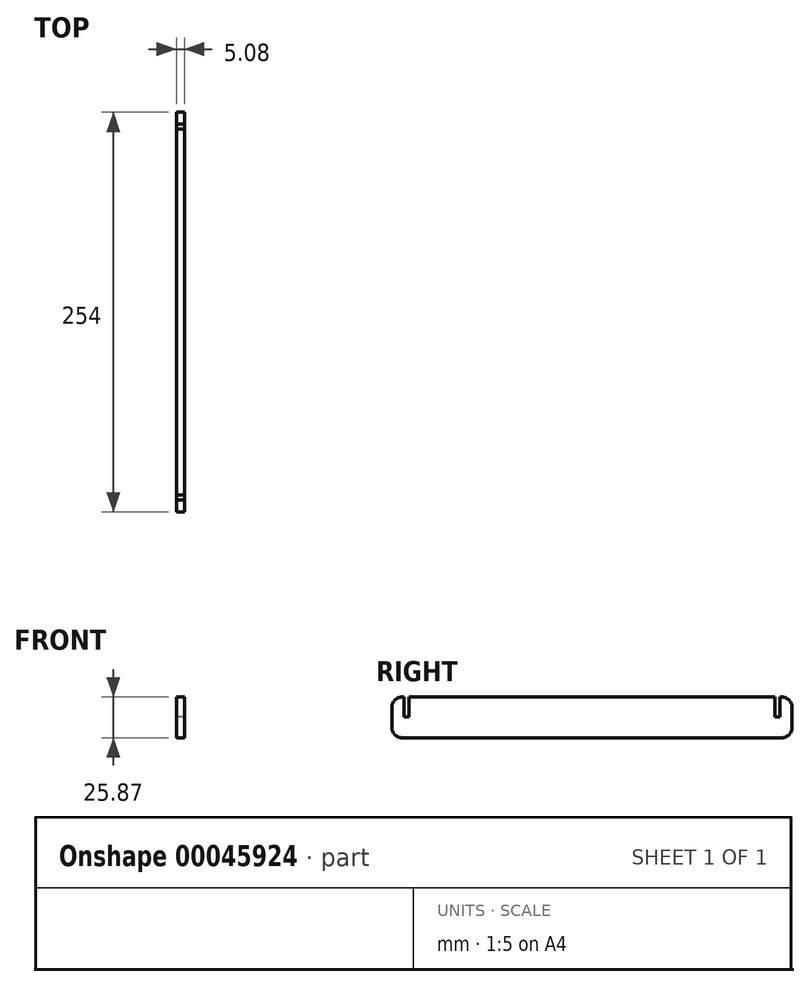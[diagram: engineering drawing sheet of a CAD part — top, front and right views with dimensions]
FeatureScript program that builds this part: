
annotation { "Feature Type Name" : "Feature", "Feature Type Description" : "" }
export const myFeature = defineFeature(function(context is Context, id is Id, definition is map)
    precondition{}
    {
        {
            var Q0;
            Q0=qCreatedBy(makeId("Right.planeOp"),FACE);
            var sketch = newSketch(context, id + "F0", { "sketchPlane" : qUnion([Q0])});
            skLineSegment(sketch, "E0.bottom", {"start": v(6.35, 0) * mm, "end": v(247.65, 0) * mm});
            skLineSegment(sketch, "E0.top", {"start": v(6.35, 25.87) * mm, "end": v(7.62, 25.87) * mm});
            skLineSegment(sketch, "E0.left", {"start": v(0, 6.35) * mm, "end": v(0, 19.52) * mm});
            skLineSegment(sketch, "E0.right", {"start": v(254, 6.35) * mm, "end": v(254, 19.52) * mm});
            skLineSegment(sketch, "E1.top", {"start": v(7.62, 13.17) * mm, "end": v(10.8, 13.17) * mm});
            skLineSegment(sketch, "E1.left", {"start": v(7.62, 25.87) * mm, "end": v(7.62, 13.17) * mm});
            skLineSegment(sketch, "E1.right", {"start": v(10.8, 25.87) * mm, "end": v(10.8, 13.17) * mm});
            skLineSegment(sketch, "E2.top", {"start": v(243.2, 13.17) * mm, "end": v(246.38, 13.17) * mm});
            skLineSegment(sketch, "E2.left", {"start": v(243.2, 25.87) * mm, "end": v(243.2, 13.17) * mm});
            skLineSegment(sketch, "E2.right", {"start": v(246.38, 25.87) * mm, "end": v(246.38, 13.17) * mm});
            skLineSegment(sketch, "E3.trimOffspring", {"start": v(10.8, 25.87) * mm, "end": v(243.2, 25.87) * mm});
            skLineSegment(sketch, "E4.trimOffspring", {"start": v(246.38, 25.87) * mm, "end": v(247.65, 25.87) * mm});
            skPoint(sketch, "E5.visualSharp", {"position": v(0, 25.87) * mm});
            skArc(sketch, "E5.filletArc", {"start": v(6.35, 25.87) * mm, "mid": v(1.86, 24) * mm, "end": v(0, 19.52) * mm});
            skPoint(sketch, "E6.visualSharp", {"position": v(0, 0) * mm});
            skArc(sketch, "E6.filletArc", {"start": v(0, 6.35) * mm, "mid": v(1.86, 1.86) * mm, "end": v(6.35, 0) * mm});
            skPoint(sketch, "E7.visualSharp", {"position": v(254, 0) * mm});
            skArc(sketch, "E7.filletArc", {"start": v(247.65, 0) * mm, "mid": v(252.14, 1.86) * mm, "end": v(254, 6.35) * mm});
            skPoint(sketch, "E8.visualSharp", {"position": v(254, 25.87) * mm});
            skArc(sketch, "E8.filletArc", {"start": v(254, 19.52) * mm, "mid": v(252.14, 24) * mm, "end": v(247.65, 25.87) * mm});
            skSolve(sketch);
        }
        {
            var Q0;
            Q0 = qSketchRegion(id + "F0", true);
            extrude(context, id + "F1", {"entities" : qUnion([Q0]), "depth" : 5.08 * mm});
        }
    });
